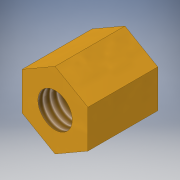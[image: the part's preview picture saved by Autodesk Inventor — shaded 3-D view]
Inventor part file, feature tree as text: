
AUTODESK INVENTOR PART (.ipt)
format: ipt  version: 2019 (Build 230136000, 136)  size: 134,144 bytes
history: native  units: mm
features: other x6, extrude x1, hole x1, sketch x1
ambient origin geometry x8: Origin, YZ Plane, XZ Plane, XY Plane, X Axis, Y Axis, Z Axis, Center Point
bodies: Solid1 (feature_tree)
feature tree (9):
  other  "Table"
  other  "Spacer-M3-FF-05"
  other  "Spacer-M3-FF-10"
  other  "Spacer-M3-FF-15"
  other  "Spacer-M3-FF-20"
  other  "Spacer-M3-FF-25"
  extrude  "Hexagon1"  Depth=5.0mm TaperAngle=0.0deg
  hole  "Hole1"  [1 undecoded]
  sketch  "Sketch1"  dims[d0=5.427093mm d1=5.0mm d2=0.0mm d27=10.0mm d28=10.0mm d5=2.459mm d6=4.0mm d7=4.4mm d8=2.0mm d9=90.0deg d10=4.5mm d11=0.0mm d20=4.7mm d21=2.713546mm]
note: 1 required parameter value undecoded (feature->parameter linkage not recoverable at this tier; creation-order binding heuristic only, values carry confidence <= 0.55)
